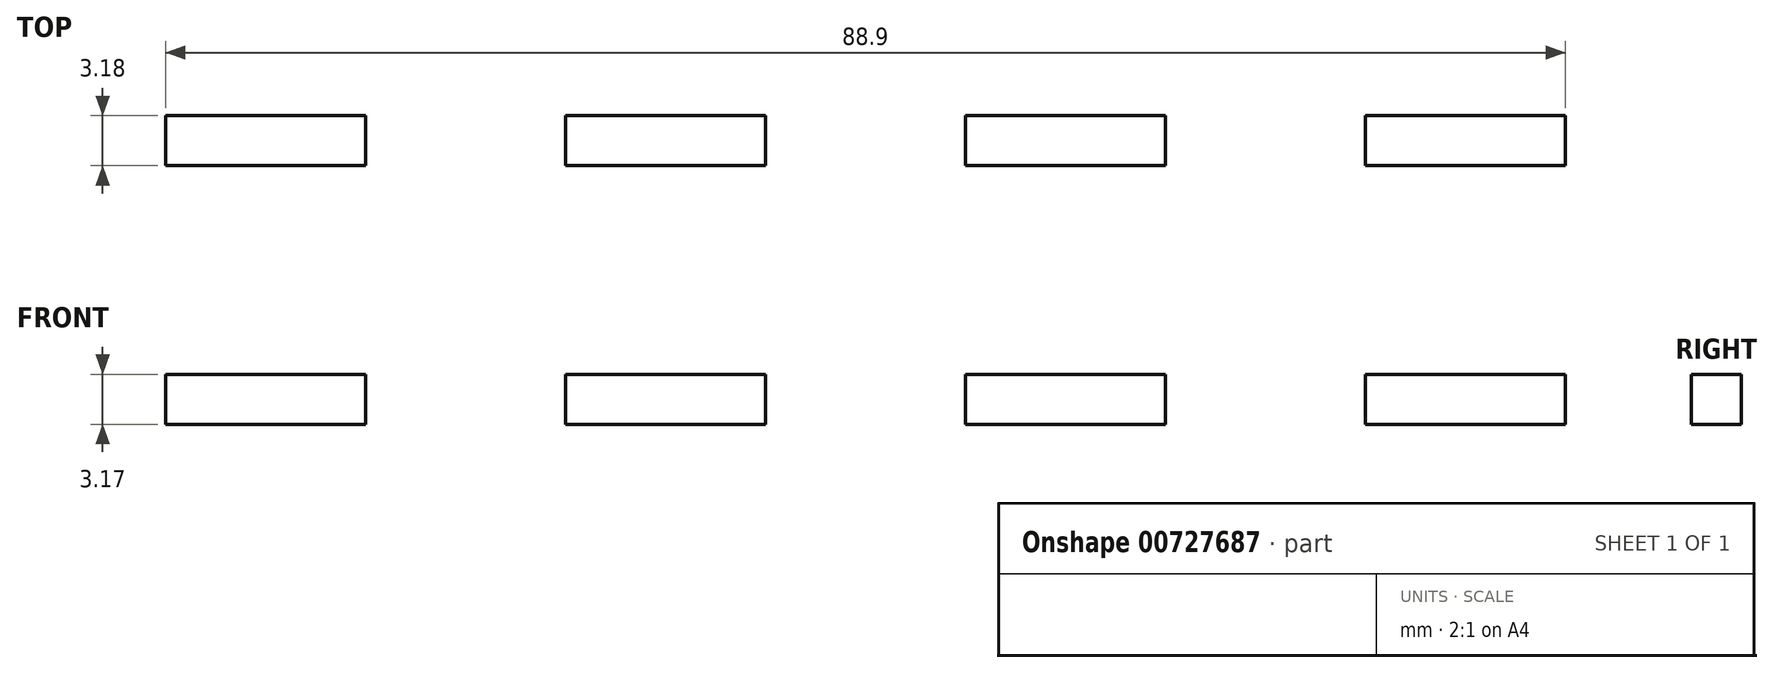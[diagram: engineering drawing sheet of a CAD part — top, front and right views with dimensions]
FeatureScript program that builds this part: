
annotation { "Feature Type Name" : "Feature", "Feature Type Description" : "" }
export const myFeature = defineFeature(function(context is Context, id is Id, definition is map)
    precondition{}
    {
        {
            var Q0;
            Q0=qCreatedBy(makeId("Top.planeOp"),FACE);
            var sketch = newSketch(context, id + "F0", { "sketchPlane" : qUnion([Q0])});
            skLineSegment(sketch, "E0.bottom", {"start": v(-88.05, 50.8) * mm, "end": v(64.35, 50.8) * mm});
            skLineSegment(sketch, "E0.top", {"start": v(-88.05, -25.4) * mm, "end": v(64.35, -25.4) * mm});
            skLineSegment(sketch, "E0.left", {"start": v(-88.05, 50.8) * mm, "end": v(-88.05, -25.4) * mm});
            skLineSegment(sketch, "E0.right", {"start": v(64.35, 50.8) * mm, "end": v(64.35, -25.4) * mm});
            skLineSegment(sketch, "E1", {"start": v(-11.85, -25.4) * mm, "end": v(-11.85, -76.2) * mm});
            skLineSegment(sketch, "E2", {"start": v(-11.85, -76.2) * mm, "end": v(-43.6, -76.2) * mm});
            skLineSegment(sketch, "E3", {"start": v(-43.6, -76.2) * mm, "end": v(-43.6, -25.4) * mm});
            skLineSegment(sketch, "E4", {"start": v(-11.85, -76.2) * mm, "end": v(19.9, -76.2) * mm});
            skLineSegment(sketch, "E5", {"start": v(19.9, -76.2) * mm, "end": v(19.9, -25.4) * mm});
            skLineSegment(sketch, "E6", {"start": v(-88.05, -25.4) * mm, "end": v(-88.05, -19.05) * mm});
            skLineSegment(sketch, "E7", {"start": v(-88.05, -19.05) * mm, "end": v(-84.87, -19.05) * mm});
            skLineSegment(sketch, "E8", {"start": v(-84.87, -19.05) * mm, "end": v(-84.87, 44.45) * mm});
            skLineSegment(sketch, "E9", {"start": v(-84.87, 44.45) * mm, "end": v(-88.05, 44.45) * mm});
            skLineSegment(sketch, "E10.MirrorCS", {"start": v(64.35, -19.05) * mm, "end": v(61.18, -19.05) * mm});
            skLineSegment(sketch, "E11.MirrorCS", {"start": v(61.18, -19.05) * mm, "end": v(61.18, 44.45) * mm});
            skLineSegment(sketch, "E12.MirrorCS", {"start": v(61.18, 44.45) * mm, "end": v(64.35, 44.45) * mm});
            skLineSegment(sketch, "E13", {"start": v(64.35, 50.8) * mm, "end": v(58, 50.8) * mm});
            skLineSegment(sketch, "E14", {"start": v(58, 50.8) * mm, "end": v(58, 47.62) * mm});
            skLineSegment(sketch, "E15", {"start": v(58, 47.62) * mm, "end": v(-81.7, 47.62) * mm});
            skLineSegment(sketch, "E16", {"start": v(-81.7, 47.62) * mm, "end": v(-81.7, 50.8) * mm});
            skLineSegment(sketch, "E17", {"start": v(-84.87, 44.45) * mm, "end": v(-84.87, 31.75) * mm});
            skLineSegment(sketch, "E18", {"start": v(-84.87, 31.75) * mm, "end": v(-88.05, 31.75) * mm});
            skLineSegment(sketch, "E19", {"start": v(-88.05, 31.75) * mm, "end": v(-88.05, 19.05) * mm});
            skLineSegment(sketch, "E20", {"start": v(-88.05, 19.05) * mm, "end": v(-84.87, 19.05) * mm});
            skLineSegment(sketch, "E21", {"start": v(-84.87, 19.05) * mm, "end": v(-84.87, 6.35) * mm});
            skLineSegment(sketch, "E22", {"start": v(-84.87, 6.35) * mm, "end": v(-88.05, 6.35) * mm});
            skLineSegment(sketch, "E23", {"start": v(-88.05, 6.35) * mm, "end": v(-88.05, -6.35) * mm});
            skLineSegment(sketch, "E24", {"start": v(-88.05, -6.35) * mm, "end": v(-84.87, -6.35) * mm});
            skLineSegment(sketch, "E25.MirrorCS", {"start": v(64.35, -6.35) * mm, "end": v(61.18, -6.35) * mm});
            skLineSegment(sketch, "E26.MirrorCS", {"start": v(61.18, 6.35) * mm, "end": v(64.35, 6.35) * mm});
            skLineSegment(sketch, "E27.MirrorCS", {"start": v(64.35, 19.05) * mm, "end": v(61.18, 19.05) * mm});
            skLineSegment(sketch, "E28.MirrorCS", {"start": v(61.18, 31.75) * mm, "end": v(64.35, 31.75) * mm});
            skLineSegment(sketch, "E29", {"start": v(-81.7, 47.62) * mm, "end": v(-56.3, 47.62) * mm});
            skLineSegment(sketch, "E30", {"start": v(-56.3, 47.62) * mm, "end": v(-56.3, 50.8) * mm});
            skLineSegment(sketch, "E31", {"start": v(-56.3, 50.8) * mm, "end": v(-30.9, 50.8) * mm});
            skLineSegment(sketch, "E32", {"start": v(-30.9, 50.8) * mm, "end": v(-30.9, 47.62) * mm});
            skLineSegment(sketch, "E33", {"start": v(-30.9, 47.62) * mm, "end": v(-18.2, 47.62) * mm});
            skLineSegment(sketch, "E34", {"start": v(-18.2, 47.62) * mm, "end": v(-18.2, 50.8) * mm});
            skLineSegment(sketch, "E35", {"start": v(-18.2, 50.8) * mm, "end": v(-5.5, 50.8) * mm});
            skLineSegment(sketch, "E36", {"start": v(-5.5, 50.8) * mm, "end": v(-5.5, 47.62) * mm});
            skLineSegment(sketch, "E37", {"start": v(-5.5, 47.62) * mm, "end": v(7.2, 47.62) * mm});
            skLineSegment(sketch, "E38", {"start": v(7.2, 47.62) * mm, "end": v(7.2, 50.8) * mm});
            skLineSegment(sketch, "E39", {"start": v(7.2, 50.8) * mm, "end": v(32.6, 50.8) * mm});
            skLineSegment(sketch, "E40", {"start": v(32.6, 50.8) * mm, "end": v(32.6, 47.62) * mm});
            skLineSegment(sketch, "E41", {"start": v(-43.6, 50.8) * mm, "end": v(-43.6, 47.62) * mm});
            skLineSegment(sketch, "E42", {"start": v(-69, 47.62) * mm, "end": v(-69, 50.8) * mm});
            skLineSegment(sketch, "E43", {"start": v(19.9, 50.8) * mm, "end": v(19.9, 47.62) * mm});
            skLineSegment(sketch, "E44", {"start": v(58, 47.62) * mm, "end": v(45.3, 47.62) * mm});
            skLineSegment(sketch, "E45", {"start": v(45.3, 47.62) * mm, "end": v(45.3, 50.8) * mm});
            skLineSegment(sketch, "E46", {"start": v(-88.05, -25.4) * mm, "end": v(-88.05, -63.5) * mm});
            skLineSegment(sketch, "E47", {"start": v(-88.05, -63.5) * mm, "end": v(-69, -63.5) * mm});
            skLineSegment(sketch, "E48", {"start": v(-69, -63.5) * mm, "end": v(-69, -25.4) * mm});
            skLineSegment(sketch, "E49", {"start": v(64.35, -25.4) * mm, "end": v(64.35, -63.5) * mm});
            skLineSegment(sketch, "E50", {"start": v(64.35, -63.5) * mm, "end": v(45.3, -63.5) * mm});
            skLineSegment(sketch, "E51", {"start": v(45.3, -63.5) * mm, "end": v(45.3, -25.4) * mm});
            skLineSegment(sketch, "E52", {"start": v(-11.85, -25.4) * mm, "end": v(-11.85, 0) * mm});
            skLineSegment(sketch, "E53", {"start": v(-11.85, 0) * mm, "end": v(39.94, 0) * mm});
            skLineSegment(sketch, "E54", {"start": v(39.94, 0) * mm, "end": v(39.94, 45) * mm});
            skLineSegment(sketch, "E55", {"start": v(39.94, 45) * mm, "end": v(-64.25, 45) * mm});
            skLineSegment(sketch, "E56", {"start": v(-64.25, 45) * mm, "end": v(-64.25, 0) * mm});
            skLineSegment(sketch, "E57", {"start": v(-64.25, 0) * mm, "end": v(-11.85, 0) * mm});
            skLineSegment(sketch, "E58", {"start": v(-69, 47.62) * mm, "end": v(-69, 0) * mm});
            skLineSegment(sketch, "E59", {"start": v(-69, 0) * mm, "end": v(-69, -2.54) * mm});
            skLineSegment(sketch, "E60.MirrorCS", {"start": v(45.3, 47.62) * mm, "end": v(45.3, 0) * mm});
            skLineSegment(sketch, "E61.MirrorCS", {"start": v(45.3, 0) * mm, "end": v(45.3, -2.54) * mm});
            skLineSegment(sketch, "E62", {"start": v(-69, -2.54) * mm, "end": v(45.3, -2.54) * mm});
            skSolve(sketch);
        }
        {
            var Q0;
            {var subQ0=sQuery(id+"F0.wireOp",EDGE,"E33");Q0=makeQuery(id+"F0.imprint","IMPRINT",FACE,{"disambiguationData":[TD([[makeQuery(id+"F0.imprint","IMPRINT",EDGE,{"derivedFrom":subQ0}),-1.0]])]});}
            var Q1;
            {var subQ0=sQuery(id+"F0.wireOp",EDGE,"E30");Q1=makeQuery(id+"F0.imprint","IMPRINT",FACE,{"disambiguationData":[TD([[makeQuery(id+"F0.imprint","IMPRINT",EDGE,{"derivedFrom":subQ0}),-1.0]])]});}
            var Q2;
            {var subQ0=sQuery(id+"F0.wireOp",EDGE,"E32");Q2=makeQuery(id+"F0.imprint","IMPRINT",FACE,{"disambiguationData":[TD([[makeQuery(id+"F0.imprint","IMPRINT",EDGE,{"derivedFrom":subQ0}),1.0]])]});}
            var Q3;
            {var subQ0=sQuery(id+"F0.wireOp",EDGE,"E36");Q3=makeQuery(id+"F0.imprint","IMPRINT",FACE,{"disambiguationData":[TD([[makeQuery(id+"F0.imprint","IMPRINT",EDGE,{"derivedFrom":subQ0}),1.0]])]});}
            var Q4;
            {var subQ0=sQuery(id+"F0.wireOp",EDGE,"E40");Q4=makeQuery(id+"F0.imprint","IMPRINT",FACE,{"disambiguationData":[TD([[makeQuery(id+"F0.imprint","IMPRINT",EDGE,{"derivedFrom":subQ0}),-1.0]])]});}
            extrude(context, id + "F1", {"entities" : qUnion([Q0, Q1, Q2, Q3, Q4]), "depth" : 3.17 * mm, "offsetDistance" : 25.4 * mm});
        }
    });
